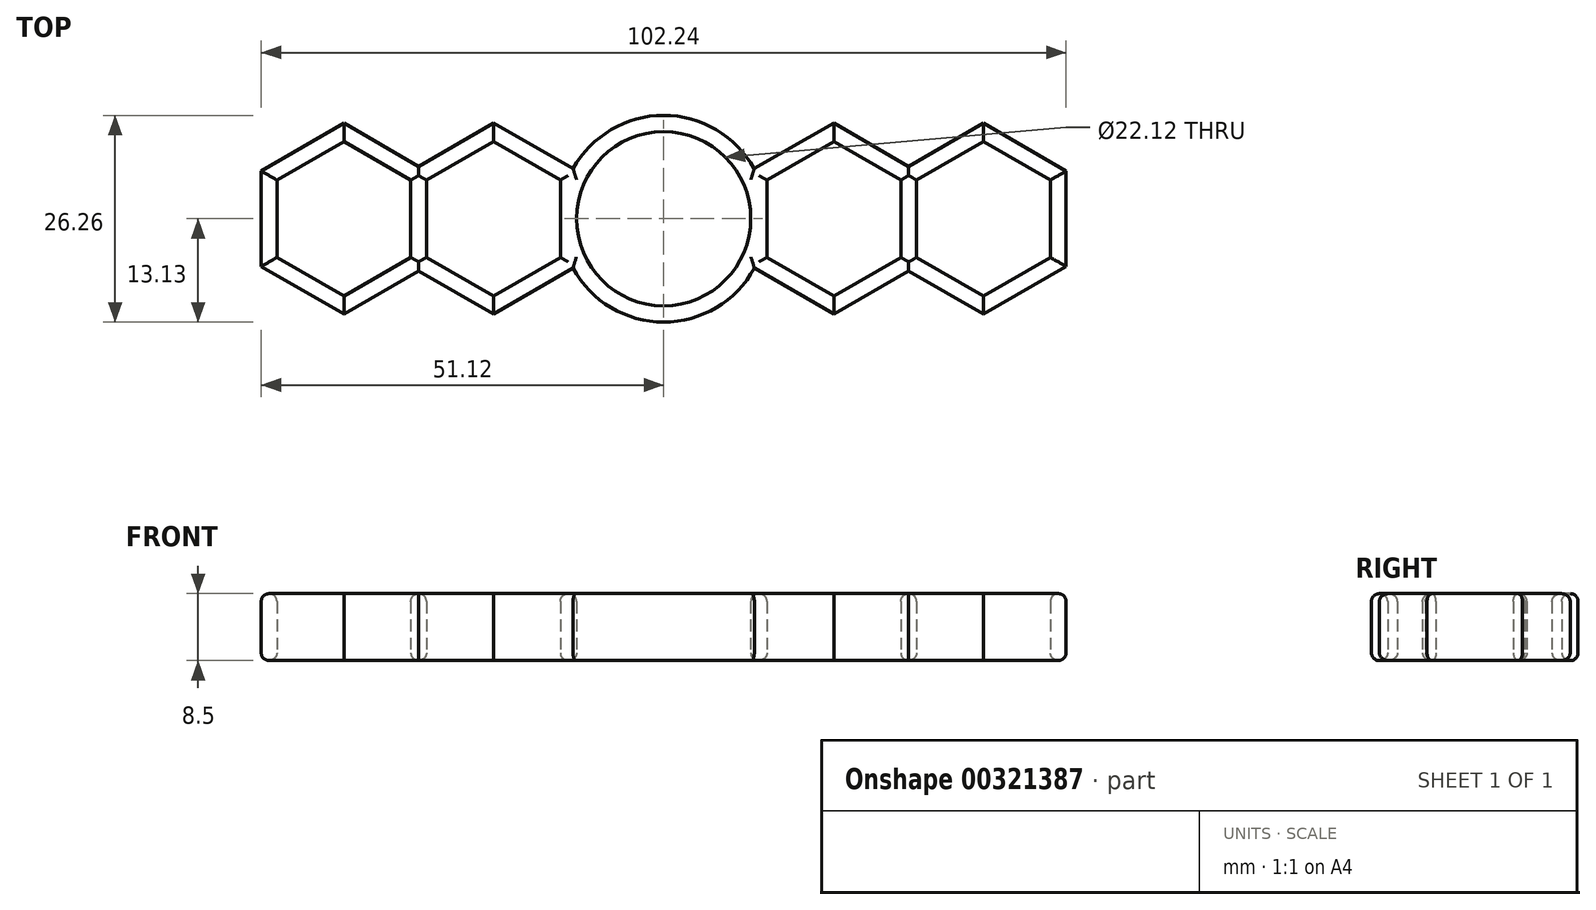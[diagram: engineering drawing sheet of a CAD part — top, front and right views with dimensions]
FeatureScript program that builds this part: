
annotation { "Feature Type Name" : "Feature", "Feature Type Description" : "" }
export const myFeature = defineFeature(function(context is Context, id is Id, definition is map)
    precondition{}
    {
        {
            var Q0;
            Q0=qCreatedBy(makeId("Top.planeOp"),FACE);
            var sketch = newSketch(context, id + "F0", { "sketchPlane" : qUnion([Q0])});
            skCircle(sketch, "E0", {"center": v(0, 0) * mm, "radius": 11.06 * mm});
            skCircle(sketch, "E1", {"center": v(0, 0) * mm, "radius": 13.12 * mm});
            skPoint(sketch, "E2", {"position": v(-11.06, 0) * mm});
            skPoint(sketch, "E3", {"position": v(-13.12, 0) * mm});
            skLineSegment(sketch, "E4", {"start": v(0, 11.06) * mm, "end": v(0, -11.06) * mm, "construction": true});
            skLineSegment(sketch, "E5.0", {"start": v(-11, 6.06) * mm, "end": v(-11.12, -6.06) * mm});
            skLineSegment(sketch, "E5.1", {"start": v(-11.12, -6.06) * mm, "end": v(-21.62, -12.12) * mm});
            skLineSegment(sketch, "E5.2", {"start": v(-21.62, -12.12) * mm, "end": v(-32.12, -6.06) * mm});
            skLineSegment(sketch, "E5.3", {"start": v(-32.12, -6.06) * mm, "end": v(-32.12, 6.06) * mm});
            skLineSegment(sketch, "E5.4", {"start": v(-32.12, 6.06) * mm, "end": v(-21.63, 12.12) * mm});
            skLineSegment(sketch, "E5.5", {"start": v(-21.63, 12.12) * mm, "end": v(-11, 6.06) * mm});
            skLineSegment(sketch, "E6.0", {"start": v(-13.12, 4.9) * mm, "end": v(-13.12, -4.9) * mm});
            skLineSegment(sketch, "E6.1", {"start": v(-13.12, -4.9) * mm, "end": v(-21.62, -9.81) * mm});
            skLineSegment(sketch, "E6.2", {"start": v(-21.62, -9.81) * mm, "end": v(-30.12, -4.9) * mm});
            skLineSegment(sketch, "E6.3", {"start": v(-30.12, -4.9) * mm, "end": v(-30.12, 4.9) * mm});
            skLineSegment(sketch, "E6.4", {"start": v(-30.12, 4.9) * mm, "end": v(-21.63, 9.81) * mm});
            skLineSegment(sketch, "E6.5", {"start": v(-21.63, 9.81) * mm, "end": v(-13.12, 4.9) * mm});
            skPoint(sketch, "E7", {"position": v(-30.12, 0) * mm});
            skLineSegment(sketch, "E8.0", {"start": v(-30.12, 6.06) * mm, "end": v(-30.12, -6.06) * mm});
            skLineSegment(sketch, "E8.1", {"start": v(-30.12, -6.06) * mm, "end": v(-40.62, -12.12) * mm});
            skLineSegment(sketch, "E8.2", {"start": v(-40.62, -12.12) * mm, "end": v(-51.13, -6.06) * mm});
            skLineSegment(sketch, "E8.3", {"start": v(-51.13, -6.06) * mm, "end": v(-51.13, 6.06) * mm});
            skLineSegment(sketch, "E8.4", {"start": v(-51.13, 6.06) * mm, "end": v(-40.63, 12.12) * mm});
            skLineSegment(sketch, "E8.5", {"start": v(-40.63, 12.12) * mm, "end": v(-30.12, 6.06) * mm});
            skLineSegment(sketch, "E9.0", {"start": v(-32.12, 4.9) * mm, "end": v(-32.12, -4.9) * mm});
            skLineSegment(sketch, "E9.1", {"start": v(-32.12, -4.9) * mm, "end": v(-40.62, -9.81) * mm});
            skLineSegment(sketch, "E9.2", {"start": v(-40.62, -9.81) * mm, "end": v(-49.12, -4.9) * mm});
            skLineSegment(sketch, "E9.3", {"start": v(-49.12, -4.9) * mm, "end": v(-49.12, 4.9) * mm});
            skLineSegment(sketch, "E9.4", {"start": v(-49.12, 4.9) * mm, "end": v(-40.63, 9.81) * mm});
            skLineSegment(sketch, "E9.5", {"start": v(-40.63, 9.81) * mm, "end": v(-32.12, 4.9) * mm});
            skPoint(sketch, "E9.0.midPoint", {"position": v(-32.12, 0) * mm});
            skLineSegment(sketch, "E10.MirrorCS", {"start": v(11, 6.06) * mm, "end": v(11.13, -6.06) * mm});
            skLineSegment(sketch, "E11.MirrorCS", {"start": v(21.63, 12.12) * mm, "end": v(11, 6.06) * mm});
            skLineSegment(sketch, "E12.MirrorCS", {"start": v(32.12, 6.06) * mm, "end": v(21.63, 12.12) * mm});
            skLineSegment(sketch, "E13.MirrorCS", {"start": v(40.63, 12.12) * mm, "end": v(30.12, 6.06) * mm});
            skLineSegment(sketch, "E14.MirrorCS", {"start": v(51.13, 6.06) * mm, "end": v(40.63, 12.12) * mm});
            skLineSegment(sketch, "E15.MirrorCS", {"start": v(51.13, -6.06) * mm, "end": v(51.13, 6.06) * mm});
            skLineSegment(sketch, "E16.MirrorCS", {"start": v(40.62, -12.12) * mm, "end": v(51.13, -6.06) * mm});
            skLineSegment(sketch, "E17.MirrorCS", {"start": v(30.12, -6.06) * mm, "end": v(40.62, -12.12) * mm});
            skLineSegment(sketch, "E18.MirrorCS", {"start": v(21.62, -12.12) * mm, "end": v(32.12, -6.06) * mm});
            skLineSegment(sketch, "E19.MirrorCS", {"start": v(11.12, -6.06) * mm, "end": v(21.63, -12.12) * mm});
            skLineSegment(sketch, "E20.MirrorCS", {"start": v(13.12, 4.9) * mm, "end": v(13.12, -4.9) * mm});
            skLineSegment(sketch, "E21.MirrorCS", {"start": v(21.63, 9.81) * mm, "end": v(13.12, 4.9) * mm});
            skLineSegment(sketch, "E22.MirrorCS", {"start": v(30.13, 4.9) * mm, "end": v(21.63, 9.81) * mm});
            skLineSegment(sketch, "E23.MirrorCS", {"start": v(30.12, -4.9) * mm, "end": v(30.12, 4.9) * mm});
            skLineSegment(sketch, "E24.MirrorCS", {"start": v(21.62, -9.81) * mm, "end": v(30.12, -4.9) * mm});
            skLineSegment(sketch, "E25.MirrorCS", {"start": v(13.12, -4.9) * mm, "end": v(21.62, -9.81) * mm});
            skLineSegment(sketch, "E26.MirrorCS", {"start": v(32.12, 4.9) * mm, "end": v(32.12, -4.9) * mm});
            skLineSegment(sketch, "E27.MirrorCS", {"start": v(40.63, 9.81) * mm, "end": v(32.12, 4.9) * mm});
            skLineSegment(sketch, "E28.MirrorCS", {"start": v(49.12, 4.9) * mm, "end": v(40.63, 9.81) * mm});
            skLineSegment(sketch, "E29.MirrorCS", {"start": v(49.12, -4.9) * mm, "end": v(49.12, 4.9) * mm});
            skLineSegment(sketch, "E30.MirrorCS", {"start": v(40.62, -9.81) * mm, "end": v(49.12, -4.9) * mm});
            skLineSegment(sketch, "E31.MirrorCS", {"start": v(32.12, -4.9) * mm, "end": v(40.62, -9.81) * mm});
            skSolve(sketch);
        }
        {
            var Q0;
            Q0 = qSketchRegion(id + "F0", true);
            extrude(context, id + "F1", {"entities" : qUnion([Q0]), "depth" : 8.5 * mm});
        }
        {
            var Q0;
            Q0=makeQuery(id+"F1.opExtrude","CAP_FACE",FACE,{"disambiguationData":[OSD([sQuery(id+"F0.wireOp",EDGE,"E0"),sQuery(id+"F0.wireOp",EDGE,"E1"),sQuery(id+"F0.wireOp",EDGE,"bb4a6209-c542-40b6-a0aa-13aee0a0b04b.0"),sQuery(id+"F0.wireOp",EDGE,"bb4a6209-c542-40b6-a0aa-13aee0a0b04b.1"),sQuery(id+"F0.wireOp",EDGE,"bb4a6209-c542-40b6-a0aa-13aee0a0b04b.2"),sQuery(id+"F0.wireOp",EDGE,"bb4a6209-c542-40b6-a0aa-13aee0a0b04b.4"),sQuery(id+"F0.wireOp",EDGE,"bb4a6209-c542-40b6-a0aa-13aee0a0b04b.5"),sQuery(id+"F0.wireOp",EDGE,"0131d484-fe6c-4ada-a321-f076c776e54c.0"),sQuery(id+"F0.wireOp",EDGE,"0131d484-fe6c-4ada-a321-f076c776e54c.1"),sQuery(id+"F0.wireOp",EDGE,"0131d484-fe6c-4ada-a321-f076c776e54c.2"),sQuery(id+"F0.wireOp",EDGE,"0131d484-fe6c-4ada-a321-f076c776e54c.4"),sQuery(id+"F0.wireOp",EDGE,"0131d484-fe6c-4ada-a321-f076c776e54c.5"),sQuery(id+"F0.wireOp",EDGE,"5aea7855-7a5f-4a02-8426-44f7e80ba7b0.0"),sQuery(id+"F0.wireOp",EDGE,"5aea7855-7a5f-4a02-8426-44f7e80ba7b0.1"),sQuery(id+"F0.wireOp",EDGE,"5aea7855-7a5f-4a02-8426-44f7e80ba7b0.2"),sQuery(id+"F0.wireOp",EDGE,"5aea7855-7a5f-4a02-8426-44f7e80ba7b0.3"),sQuery(id+"F0.wireOp",EDGE,"5aea7855-7a5f-4a02-8426-44f7e80ba7b0.4"),sQuery(id+"F0.wireOp",EDGE,"5aea7855-7a5f-4a02-8426-44f7e80ba7b0.5"),sQuery(id+"F0.wireOp",EDGE,"9ece3242-d8ee-468a-8903-69ce3de710af.0"),sQuery(id+"F0.wireOp",EDGE,"9ece3242-d8ee-468a-8903-69ce3de710af.1"),sQuery(id+"F0.wireOp",EDGE,"9ece3242-d8ee-468a-8903-69ce3de710af.2"),sQuery(id+"F0.wireOp",EDGE,"9ece3242-d8ee-468a-8903-69ce3de710af.3"),sQuery(id+"F0.wireOp",EDGE,"9ece3242-d8ee-468a-8903-69ce3de710af.4"),sQuery(id+"F0.wireOp",EDGE,"9ece3242-d8ee-468a-8903-69ce3de710af.5"),sQuery(id+"F0.wireOp",EDGE,"5af26363-9f52-4fa3-99b2-37463c5845500.MirrorCS"),sQuery(id+"F0.wireOp",EDGE,"b9d5e40f-b2dd-4261-a146-3cabcca61bf50.MirrorCS"),sQuery(id+"F0.wireOp",EDGE,"616710dd-5f1d-4a89-981f-7390ae07656f0.MirrorCS"),sQuery(id+"F0.wireOp",EDGE,"8a0f4083-b9cb-463a-a29f-879238c6be9d0.MirrorCS"),sQuery(id+"F0.wireOp",EDGE,"422bb891-a30b-44f8-8b82-786da660d0a40.MirrorCS"),sQuery(id+"F0.wireOp",EDGE,"38860732-86e6-4d54-adf1-0b68ca11e3d20.MirrorCS"),sQuery(id+"F0.wireOp",EDGE,"1cf60fe6-6e1e-4026-b869-0aed9c27b8880.MirrorCS"),sQuery(id+"F0.wireOp",EDGE,"d9ed797f-0ab6-4384-ac19-6e364def58080.MirrorCS"),sQuery(id+"F0.wireOp",EDGE,"97db681f-baa5-4f0a-86d7-2b4570bdc5e20.MirrorCS"),sQuery(id+"F0.wireOp",EDGE,"0204579e-41f4-4465-b2b6-b59cb30f4bed0.MirrorCS"),sQuery(id+"F0.wireOp",EDGE,"fdbf8a3a-e0f8-49d8-9631-1cd5b05315ff0.MirrorCS"),sQuery(id+"F0.wireOp",EDGE,"c084779e-5ca7-4c01-ac3e-d8108b3d0c290.MirrorCS"),sQuery(id+"F0.wireOp",EDGE,"90d7df44-14aa-484b-adef-4a3dce8c0a360.MirrorCS"),sQuery(id+"F0.wireOp",EDGE,"dc3c98a9-a683-45c1-ab9b-6304b0ae68be0.MirrorCS"),sQuery(id+"F0.wireOp",EDGE,"dd45e3e2-e44d-4cb6-a307-9340a6bef7c40.MirrorCS"),sQuery(id+"F0.wireOp",EDGE,"7a9f3fc9-320d-4430-9b75-ab1291d1df1e0.MirrorCS"),sQuery(id+"F0.wireOp",EDGE,"fead9b2d-86cf-44d3-9671-d88cfdff78820.MirrorCS"),sQuery(id+"F0.wireOp",EDGE,"d79eda56-f30b-4f68-9c80-66c1119cadfb0.MirrorCS"),sQuery(id+"F0.wireOp",EDGE,"a0975f0f-76df-4af0-9791-55a261aa1c500.MirrorCS"),sQuery(id+"F0.wireOp",EDGE,"ce592e1f-375d-49b0-9f14-7c14e30199ac0.MirrorCS"),sQuery(id+"F0.wireOp",EDGE,"f804c4b1-3cf8-4dd4-8396-58d551259d9f0.MirrorCS"),sQuery(id+"F0.wireOp",EDGE,"784dce3a-bb99-4dfe-aff1-9bace5f1aa1a0.MirrorCS")])],"isStart":false});
            var Q1;
            Q1=makeQuery(id+"F1.opExtrude","CAP_FACE",FACE,{"disambiguationData":[OSD([sQuery(id+"F0.wireOp",EDGE,"E0"),sQuery(id+"F0.wireOp",EDGE,"E1"),sQuery(id+"F0.wireOp",EDGE,"bb4a6209-c542-40b6-a0aa-13aee0a0b04b.0"),sQuery(id+"F0.wireOp",EDGE,"bb4a6209-c542-40b6-a0aa-13aee0a0b04b.1"),sQuery(id+"F0.wireOp",EDGE,"bb4a6209-c542-40b6-a0aa-13aee0a0b04b.2"),sQuery(id+"F0.wireOp",EDGE,"bb4a6209-c542-40b6-a0aa-13aee0a0b04b.4"),sQuery(id+"F0.wireOp",EDGE,"bb4a6209-c542-40b6-a0aa-13aee0a0b04b.5"),sQuery(id+"F0.wireOp",EDGE,"0131d484-fe6c-4ada-a321-f076c776e54c.0"),sQuery(id+"F0.wireOp",EDGE,"0131d484-fe6c-4ada-a321-f076c776e54c.1"),sQuery(id+"F0.wireOp",EDGE,"0131d484-fe6c-4ada-a321-f076c776e54c.2"),sQuery(id+"F0.wireOp",EDGE,"0131d484-fe6c-4ada-a321-f076c776e54c.4"),sQuery(id+"F0.wireOp",EDGE,"0131d484-fe6c-4ada-a321-f076c776e54c.5"),sQuery(id+"F0.wireOp",EDGE,"5aea7855-7a5f-4a02-8426-44f7e80ba7b0.0"),sQuery(id+"F0.wireOp",EDGE,"5aea7855-7a5f-4a02-8426-44f7e80ba7b0.1"),sQuery(id+"F0.wireOp",EDGE,"5aea7855-7a5f-4a02-8426-44f7e80ba7b0.2"),sQuery(id+"F0.wireOp",EDGE,"5aea7855-7a5f-4a02-8426-44f7e80ba7b0.3"),sQuery(id+"F0.wireOp",EDGE,"5aea7855-7a5f-4a02-8426-44f7e80ba7b0.4"),sQuery(id+"F0.wireOp",EDGE,"5aea7855-7a5f-4a02-8426-44f7e80ba7b0.5"),sQuery(id+"F0.wireOp",EDGE,"9ece3242-d8ee-468a-8903-69ce3de710af.0"),sQuery(id+"F0.wireOp",EDGE,"9ece3242-d8ee-468a-8903-69ce3de710af.1"),sQuery(id+"F0.wireOp",EDGE,"9ece3242-d8ee-468a-8903-69ce3de710af.2"),sQuery(id+"F0.wireOp",EDGE,"9ece3242-d8ee-468a-8903-69ce3de710af.3"),sQuery(id+"F0.wireOp",EDGE,"9ece3242-d8ee-468a-8903-69ce3de710af.4"),sQuery(id+"F0.wireOp",EDGE,"9ece3242-d8ee-468a-8903-69ce3de710af.5"),sQuery(id+"F0.wireOp",EDGE,"5af26363-9f52-4fa3-99b2-37463c5845500.MirrorCS"),sQuery(id+"F0.wireOp",EDGE,"b9d5e40f-b2dd-4261-a146-3cabcca61bf50.MirrorCS"),sQuery(id+"F0.wireOp",EDGE,"616710dd-5f1d-4a89-981f-7390ae07656f0.MirrorCS"),sQuery(id+"F0.wireOp",EDGE,"8a0f4083-b9cb-463a-a29f-879238c6be9d0.MirrorCS"),sQuery(id+"F0.wireOp",EDGE,"422bb891-a30b-44f8-8b82-786da660d0a40.MirrorCS"),sQuery(id+"F0.wireOp",EDGE,"38860732-86e6-4d54-adf1-0b68ca11e3d20.MirrorCS"),sQuery(id+"F0.wireOp",EDGE,"1cf60fe6-6e1e-4026-b869-0aed9c27b8880.MirrorCS"),sQuery(id+"F0.wireOp",EDGE,"d9ed797f-0ab6-4384-ac19-6e364def58080.MirrorCS"),sQuery(id+"F0.wireOp",EDGE,"97db681f-baa5-4f0a-86d7-2b4570bdc5e20.MirrorCS"),sQuery(id+"F0.wireOp",EDGE,"0204579e-41f4-4465-b2b6-b59cb30f4bed0.MirrorCS"),sQuery(id+"F0.wireOp",EDGE,"fdbf8a3a-e0f8-49d8-9631-1cd5b05315ff0.MirrorCS"),sQuery(id+"F0.wireOp",EDGE,"c084779e-5ca7-4c01-ac3e-d8108b3d0c290.MirrorCS"),sQuery(id+"F0.wireOp",EDGE,"90d7df44-14aa-484b-adef-4a3dce8c0a360.MirrorCS"),sQuery(id+"F0.wireOp",EDGE,"dc3c98a9-a683-45c1-ab9b-6304b0ae68be0.MirrorCS"),sQuery(id+"F0.wireOp",EDGE,"dd45e3e2-e44d-4cb6-a307-9340a6bef7c40.MirrorCS"),sQuery(id+"F0.wireOp",EDGE,"7a9f3fc9-320d-4430-9b75-ab1291d1df1e0.MirrorCS"),sQuery(id+"F0.wireOp",EDGE,"fead9b2d-86cf-44d3-9671-d88cfdff78820.MirrorCS"),sQuery(id+"F0.wireOp",EDGE,"d79eda56-f30b-4f68-9c80-66c1119cadfb0.MirrorCS"),sQuery(id+"F0.wireOp",EDGE,"a0975f0f-76df-4af0-9791-55a261aa1c500.MirrorCS"),sQuery(id+"F0.wireOp",EDGE,"ce592e1f-375d-49b0-9f14-7c14e30199ac0.MirrorCS"),sQuery(id+"F0.wireOp",EDGE,"f804c4b1-3cf8-4dd4-8396-58d551259d9f0.MirrorCS"),sQuery(id+"F0.wireOp",EDGE,"784dce3a-bb99-4dfe-aff1-9bace5f1aa1a0.MirrorCS")])],"isStart":true});
            fillet(context, id + "F2", {"entities" : qUnion([Q0, Q1]), "radius" : 1 * mm, "tangentPropagation" : true, "allowEdgeOverflow" : false});
        }
    });
